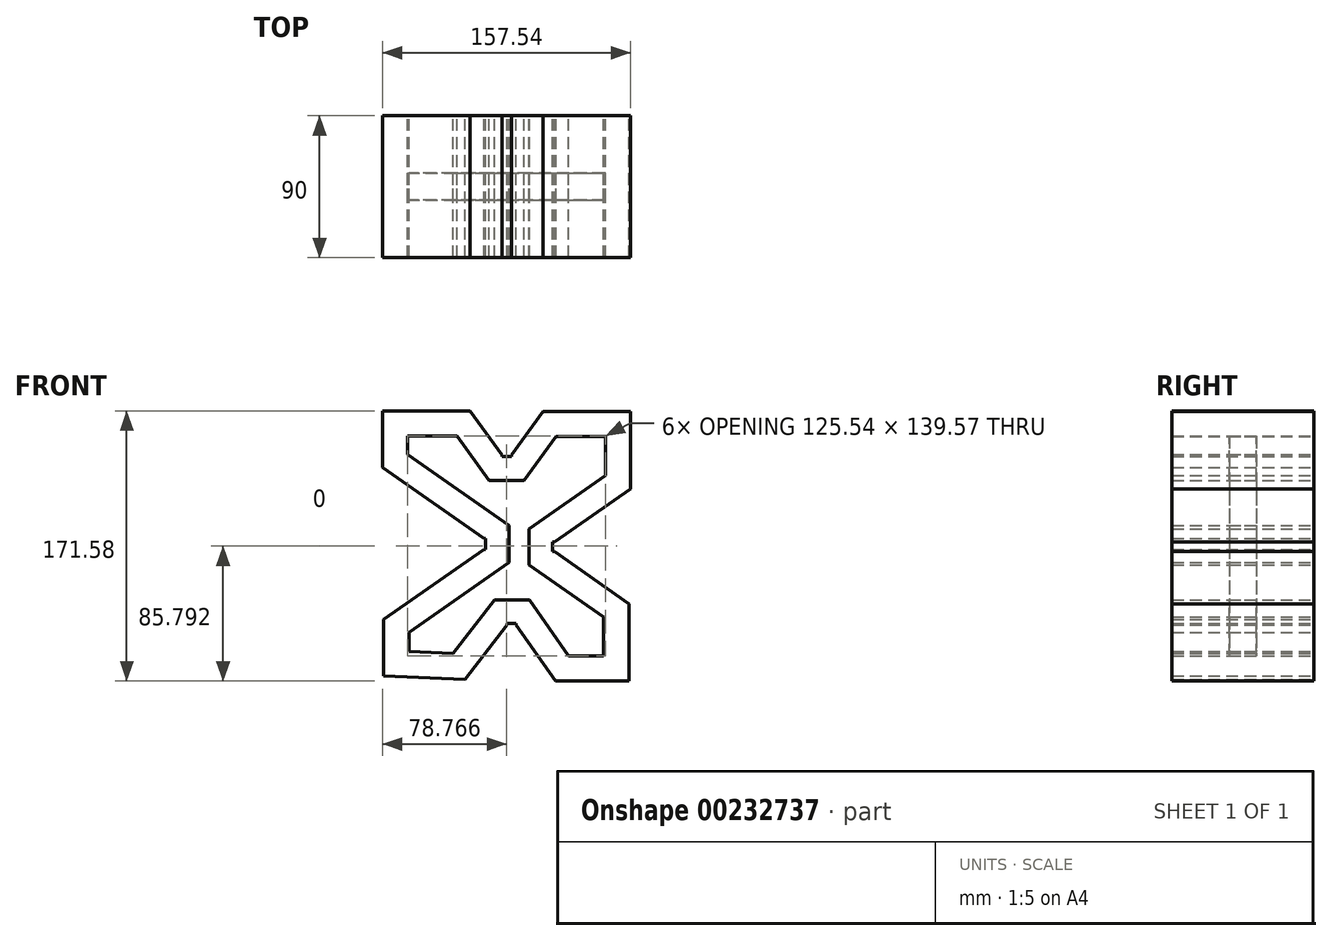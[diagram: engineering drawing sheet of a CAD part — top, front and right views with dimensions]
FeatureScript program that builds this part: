
annotation { "Feature Type Name" : "Feature", "Feature Type Description" : "" }
export const myFeature = defineFeature(function(context is Context, id is Id, definition is map)
    precondition{}
    {
        {
            var Q0;
            Q0=qCreatedBy(makeId("Front.planeOp"),FACE);
            var sketch = newSketch(context, id + "F0", { "sketchPlane" : qUnion([Q0])});
            skLineSegment(sketch, "E0", {"start": v(-80.67, 70.67) * mm, "end": v(-25.17, 70.67) * mm});
            skLineSegment(sketch, "E1", {"start": v(-25.17, 70.67) * mm, "end": v(-4.84, 42.68) * mm});
            skLineSegment(sketch, "E2", {"start": v(-4.84, 42.68) * mm, "end": v(1.16, 42.68) * mm});
            skLineSegment(sketch, "E3", {"start": v(1.16, 42.68) * mm, "end": v(21.27, 70.35) * mm});
            skLineSegment(sketch, "E4", {"start": v(21.27, 70.35) * mm, "end": v(76.87, 70.35) * mm});
            skLineSegment(sketch, "E5", {"start": v(-80.67, 70.67) * mm, "end": v(-80.67, 34.77) * mm});
            skLineSegment(sketch, "E6", {"start": v(-80.67, 34.77) * mm, "end": v(-16.29, -10.31) * mm});
            skLineSegment(sketch, "E7", {"start": v(-16.29, -10.31) * mm, "end": v(-16.29, -17.21) * mm});
            skLineSegment(sketch, "E8", {"start": v(-16.29, -17.21) * mm, "end": v(-79.85, -61.72) * mm});
            skLineSegment(sketch, "E9", {"start": v(-79.85, -61.72) * mm, "end": v(-79.85, -97.52) * mm});
            skLineSegment(sketch, "E10", {"start": v(76.87, 70.35) * mm, "end": v(76.87, 21.25) * mm});
            skLineSegment(sketch, "E11", {"start": v(76.87, 21.25) * mm, "end": v(28.45, -12.65) * mm});
            skLineSegment(sketch, "E12", {"start": v(28.45, -12.65) * mm, "end": v(28.45, -18.65) * mm});
            skLineSegment(sketch, "E13", {"start": v(28.45, -18.65) * mm, "end": v(75.8, -51.8) * mm});
            skLineSegment(sketch, "E14", {"start": v(75.8, -51.8) * mm, "end": v(75.8, -100.9) * mm});
            skLineSegment(sketch, "E15", {"start": v(75.8, -100.9) * mm, "end": v(29.3, -100.9) * mm});
            skLineSegment(sketch, "E16", {"start": v(29.3, -100.9) * mm, "end": v(4.3, -65.2) * mm});
            skLineSegment(sketch, "E17", {"start": v(4.3, -65.2) * mm, "end": v(-1.7, -65.2) * mm});
            skLineSegment(sketch, "E18", {"start": v(-1.7, -65.2) * mm, "end": v(-28.15, -99.73) * mm});
            skLineSegment(sketch, "E19", {"start": v(-28.15, -99.73) * mm, "end": v(-79.85, -97.52) * mm});
            skLineSegment(sketch, "E20.0", {"start": v(29.42, 54.35) * mm, "end": v(60.87, 54.35) * mm});
            skLineSegment(sketch, "E20.1", {"start": v(9.32, 26.68) * mm, "end": v(29.42, 54.35) * mm});
            skLineSegment(sketch, "E20.2", {"start": v(-12.99, 26.68) * mm, "end": v(9.32, 26.68) * mm});
            skLineSegment(sketch, "E20.3", {"start": v(-33.33, 54.67) * mm, "end": v(-12.99, 26.68) * mm});
            skLineSegment(sketch, "E20.4", {"start": v(-64.67, 54.67) * mm, "end": v(-33.33, 54.67) * mm});
            skLineSegment(sketch, "E20.5", {"start": v(60.87, 54.35) * mm, "end": v(60.87, 29.57) * mm});
            skLineSegment(sketch, "E20.6", {"start": v(-64.67, 54.67) * mm, "end": v(-64.67, 43.1) * mm});
            skLineSegment(sketch, "E20.7", {"start": v(-64.67, 43.1) * mm, "end": v(-0.29, -1.98) * mm});
            skLineSegment(sketch, "E20.8", {"start": v(-0.29, -1.98) * mm, "end": v(-0.29, -25.54) * mm});
            skLineSegment(sketch, "E20.9", {"start": v(-0.29, -25.54) * mm, "end": v(-63.85, -70.05) * mm});
            skLineSegment(sketch, "E20.10", {"start": v(59.8, -60.13) * mm, "end": v(59.8, -84.9) * mm});
            skLineSegment(sketch, "E20.11", {"start": v(12.45, -26.98) * mm, "end": v(59.8, -60.13) * mm});
            skLineSegment(sketch, "E20.12", {"start": v(12.45, -4.32) * mm, "end": v(12.45, -26.98) * mm});
            skLineSegment(sketch, "E20.13", {"start": v(60.87, 29.57) * mm, "end": v(12.45, -4.32) * mm});
            skLineSegment(sketch, "E20.14", {"start": v(59.8, -84.9) * mm, "end": v(37.63, -84.9) * mm});
            skLineSegment(sketch, "E20.15", {"start": v(37.63, -84.9) * mm, "end": v(12.62, -49.2) * mm});
            skLineSegment(sketch, "E20.16", {"start": v(12.62, -49.2) * mm, "end": v(-9.6, -49.2) * mm});
            skLineSegment(sketch, "E20.17", {"start": v(-9.6, -49.2) * mm, "end": v(-35.8, -83.39) * mm});
            skLineSegment(sketch, "E20.18", {"start": v(-35.8, -83.39) * mm, "end": v(-63.85, -82.2) * mm});
            skLineSegment(sketch, "E20.19", {"start": v(-63.85, -70.05) * mm, "end": v(-63.85, -82.2) * mm});
            skSolve(sketch);
        }
        {
            var Q0;
            Q0 = qSketchRegion(id + "F0", true);
            extrude(context, id + "F1", {"entities" : qUnion([Q0]), "endBound" : BoundingType.SYMMETRIC, "depth" : 90 * mm});
        }
        {
            var Q0;
            Q0=makeQuery(id+"F0.imprint","IMPRINT",FACE,{"disambiguationData":[TD([[makeQuery(id+"F0.imprint","IMPRINT",EDGE,{"derivedFrom":sQuery(id+"F0.wireOp",EDGE,"E20.0")}),-1.0]])]});
            extrude(context, id + "F2", {"entities" : qUnion([Q0]), "endBound" : BoundingType.SYMMETRIC, "depth" : 17.2 * mm});
        }
        {
            var Q0;
            Q0=makeQuery(id+"F1.opExtrude","SWEPT_FACE",FACE,{"disambiguationData":[OSD([sQuery(id+"F0.wireOp",EDGE,"E2")])]});
            extrude(context, id + "F3", {"entities" : qUnion([Q0]), "operationType" : NewBodyOperationType.REMOVE, "oppositeDirection" : true, "depth" : 1 * mm});
        }
        {
            var Q0;
            Q0=makeQuery(id+"F1.opExtrude","SWEPT_FACE",FACE,{"disambiguationData":[OSD([sQuery(id+"F0.wireOp",EDGE,"E7")])]});
            extrude(context, id + "F4", {"entities" : qUnion([Q0]), "operationType" : NewBodyOperationType.REMOVE, "oppositeDirection" : true, "depth" : 1 * mm});
        }
        {
            var Q0;
            Q0=makeQuery(id+"F1.opExtrude","SWEPT_FACE",FACE,{"disambiguationData":[OSD([sQuery(id+"F0.wireOp",EDGE,"E12")])]});
            extrude(context, id + "F5", {"entities" : qUnion([Q0]), "operationType" : NewBodyOperationType.REMOVE, "oppositeDirection" : true, "depth" : 1 * mm});
        }
        {
            var Q0;
            Q0=makeQuery(id+"F1.opExtrude","SWEPT_FACE",FACE,{"disambiguationData":[OSD([sQuery(id+"F0.wireOp",EDGE,"E17")])]});
            extrude(context, id + "F6", {"entities" : qUnion([Q0]), "operationType" : NewBodyOperationType.REMOVE, "oppositeDirection" : true, "depth" : 1 * mm});
        }
    });
